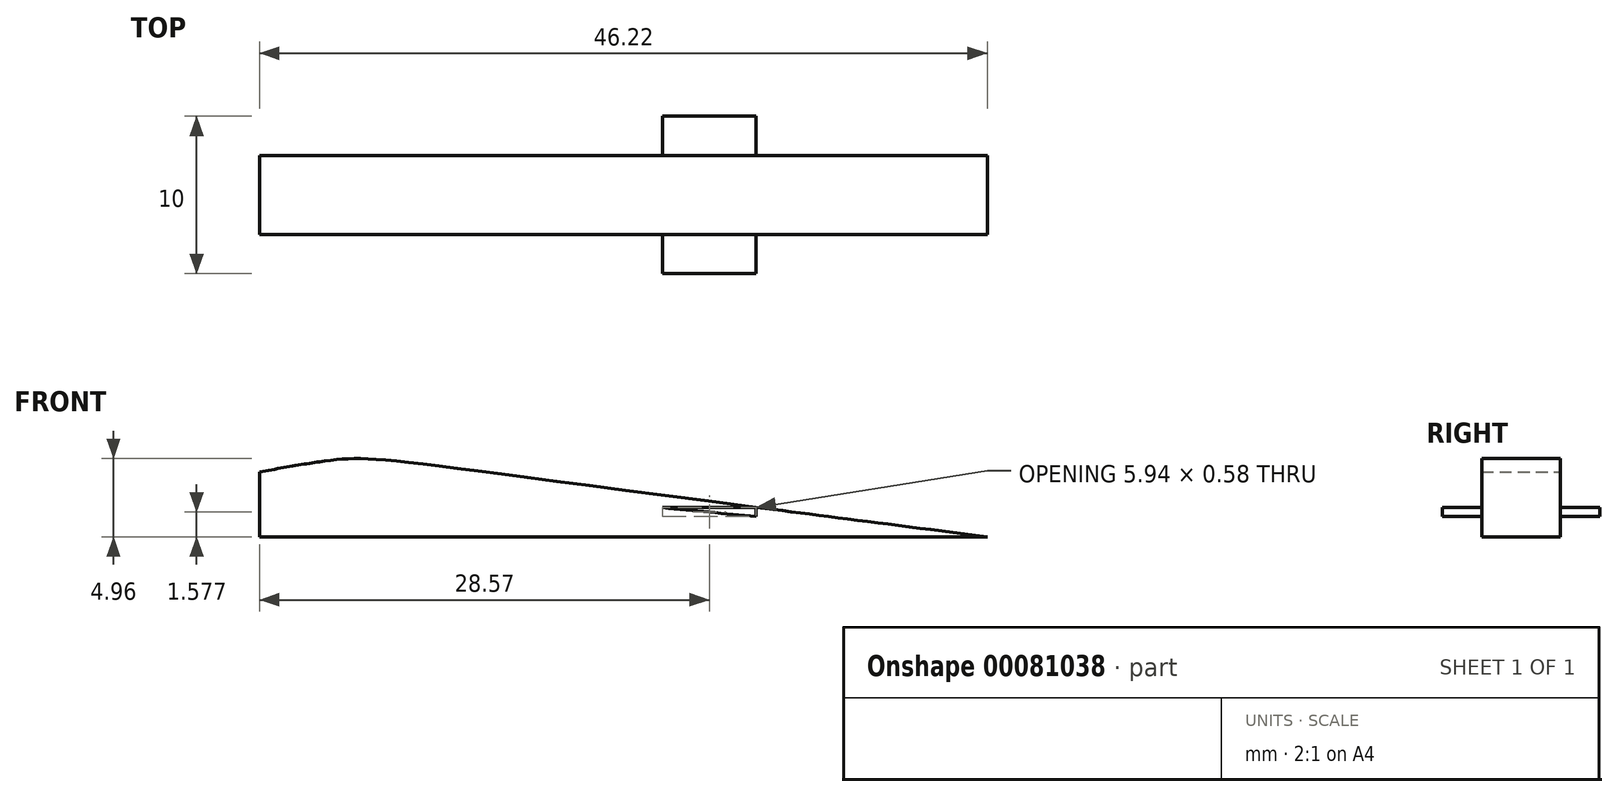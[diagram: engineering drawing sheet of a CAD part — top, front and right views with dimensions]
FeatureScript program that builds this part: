
annotation { "Feature Type Name" : "Feature", "Feature Type Description" : "" }
export const myFeature = defineFeature(function(context is Context, id is Id, definition is map)
    precondition{}
    {
        {
            var Q0;
            Q0=qCreatedBy(makeId("Front.planeOp"),FACE);
            var sketch = newSketch(context, id + "F0", { "sketchPlane" : qUnion([Q0])});
            skLineSegment(sketch, "E0", {"start": v(0, 0) * mm, "end": v(-60, 0) * mm});
            skLineSegment(sketch, "E1", {"start": v(-60, 0) * mm, "end": v(-43.5, 0) * mm});
            skLineSegment(sketch, "E2", {"start": v(-43.5, 0) * mm, "end": v(-43.5, 4.8) * mm});
            skLineSegment(sketch, "E3", {"start": v(-43.5, 0) * mm, "end": v(-51.75, 0) * mm});
            skLineSegment(sketch, "E4", {"start": v(-43.5, 0) * mm, "end": v(-47.62, 0) * mm});
            skLineSegment(sketch, "E5", {"start": v(-60, 0) * mm, "end": v(-51.75, 0) * mm});
            skLineSegment(sketch, "E6", {"start": v(-60, 0) * mm, "end": v(-55.87, 0) * mm});
            skLineSegment(sketch, "E7", {"start": v(-47.62, 0) * mm, "end": v(-47.62, 4.1) * mm});
            skLineSegment(sketch, "E8", {"start": v(-51.75, 0) * mm, "end": v(-51.75, 3.1) * mm});
            skLineSegment(sketch, "E9", {"start": v(-55.87, 0) * mm, "end": v(-55.87, 1.9) * mm});
            skFitSpline(sketch, "E10", {"points": [v(-60, 0) * mm, v(-55.87, 1.9) * mm, v(-51.75, 3.1) * mm, v(-47.62, 4.1) * mm, v(-43.5, 4.8) * mm, v(-1.4, 0) * mm], "startDerivative": vector(28.62, 14.09) * mm, "endDerivative": vector(266.32, -33.45) * mm});
            skSolve(sketch);
        }
        {
            var Q0;
            {var subQ0=sQuery(id+"F0.wireOp",EDGE,"E2");Q0=makeQuery(id+"F0.imprint","IMPRINT",FACE,{"disambiguationData":[TD([[makeQuery(id+"F0.imprint","IMPRINT",EDGE,{"derivedFrom":subQ0}),-1.0]])]});}
            var Q1;
            {var subQ0=sQuery(id+"F0.wireOp",EDGE,"E2");Q1=makeQuery(id+"F0.imprint","IMPRINT",FACE,{"disambiguationData":[TD([[makeQuery(id+"F0.imprint","IMPRINT",EDGE,{"derivedFrom":subQ0}),1.0]])]});}
            var Q2;
            Q2=makeQuery(id+"F0.imprint","IMPRINT",FACE,{"disambiguationData":[TD([[makeQuery(id+"F0.imprint","IMPRINT",EDGE,{"derivedFrom":sQuery(id+"F0.wireOp",EDGE,"E3")}),-1.0]])]});
            var Q3;
            Q3=makeQuery(id+"F0.imprint","IMPRINT",FACE,{"disambiguationData":[TD([[makeQuery(id+"F0.imprint","IMPRINT",EDGE,{"derivedFrom":sQuery(id+"F0.wireOp",EDGE,"E5")}),1.0]])]});
            var Q4;
            {var subQ0=sQuery(id+"F0.wireOp",EDGE,"E6");Q4=makeQuery(id+"F0.imprint","IMPRINT",FACE,{"disambiguationData":[TD([[makeQuery(id+"F0.imprint","IMPRINT",EDGE,{"derivedFrom":subQ0}),1.0]])]});}
            extrude(context, id + "F1", {"entities" : qUnion([Q0, Q1, Q2, Q3, Q4]), "endBound" : BoundingType.SYMMETRIC, "depth" : 5 * mm});
        }
        {
            var Q0;
            Q0=qCreatedBy(makeId("Front.planeOp"),FACE);
            var sketch = newSketch(context, id + "F2", { "sketchPlane" : qUnion([Q0])});
            skLineSegment(sketch, "E11.0", {"start": v(-1.4, 0) * mm, "end": v(-60, 0) * mm});
            skFitSpline(sketch, "E12.0", {"points": [v(-60, 0) * mm, v(-58.63, 0.68) * mm, v(-55.95, 2.06) * mm, v(-51.72, 3.1) * mm, v(-47.75, 4.15) * mm, v(-39.7, 5.42) * mm, v(-40.4, 4.9) * mm, v(-1.4, 0) * mm]});
            skLineSegment(sketch, "E13", {"start": v(-56.36, 1.71) * mm, "end": v(-16.09, 1.87) * mm});
            skLineSegment(sketch, "E14", {"start": v(-16.09, 1.87) * mm, "end": v(-16.09, 0) * mm});
            skLineSegment(sketch, "E15", {"start": v(-56.36, 1.71) * mm, "end": v(-56.35, 0) * mm});
            skSolve(sketch);
        }
        {
            var Q0;
            Q0=makeQuery(id+"F2.imprint","IMPRINT",FACE,{"disambiguationData":[TD([[makeQuery(id+"F2.imprint","IMPRINT",EDGE,{"derivedFrom":sQuery(id+"F2.wireOp",EDGE,"E13")}),-1.0]])]});
            extrude(context, id + "F3", {"entities" : qUnion([Q0]), "operationType" : NewBodyOperationType.ADD, "endBound" : BoundingType.SYMMETRIC, "depth" : 10 * mm});
        }
    });
